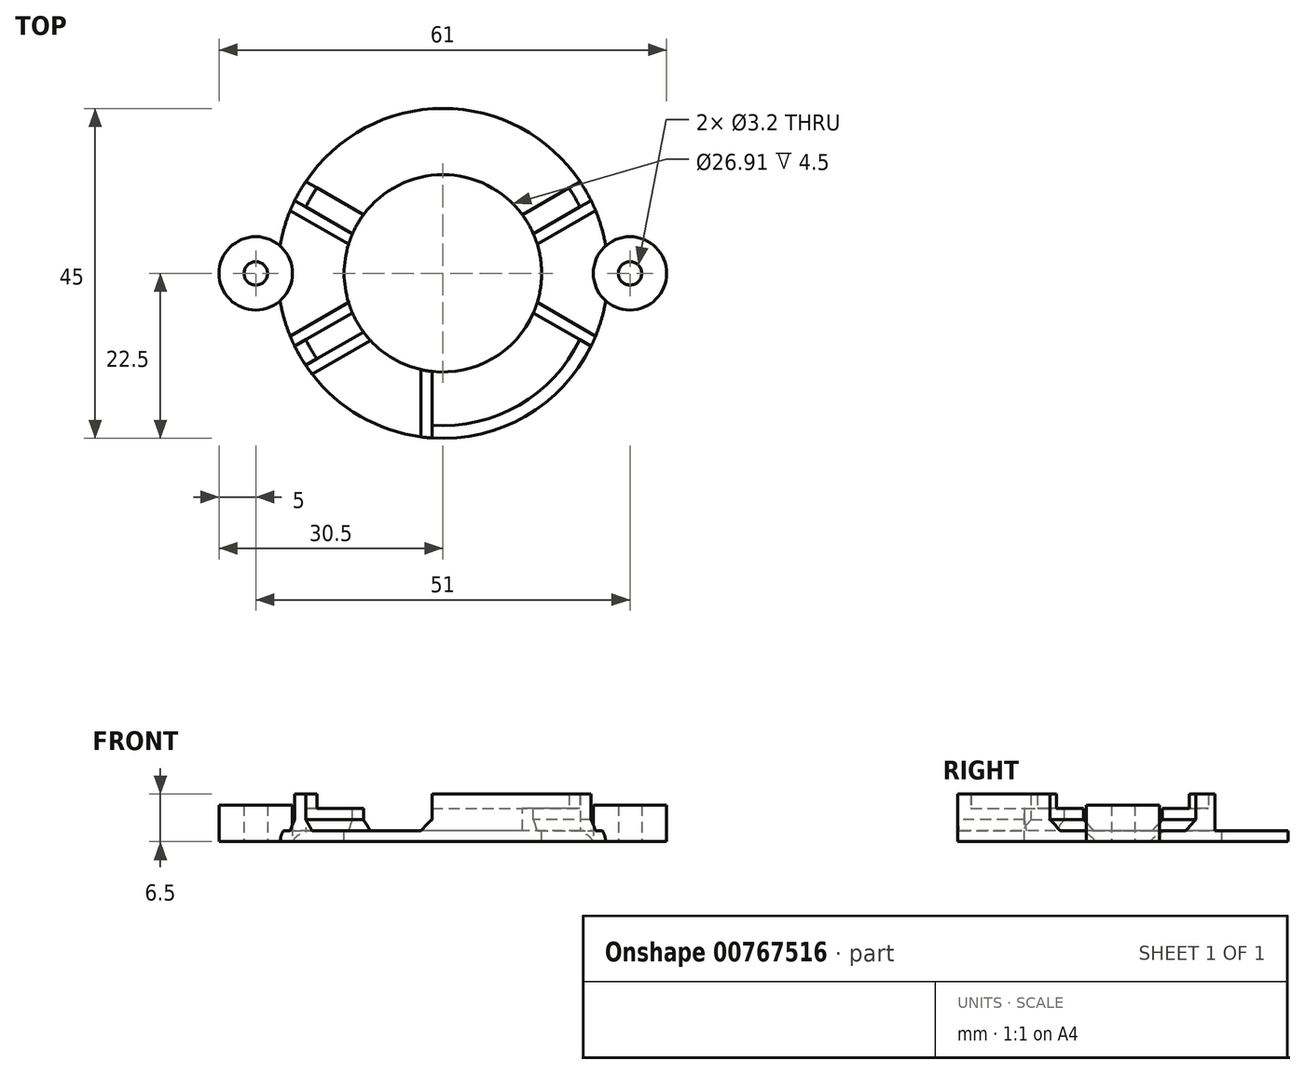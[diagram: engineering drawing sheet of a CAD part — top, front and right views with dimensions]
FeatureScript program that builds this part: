
annotation { "Feature Type Name" : "Feature", "Feature Type Description" : "" }
export const myFeature = defineFeature(function(context is Context, id is Id, definition is map)
    precondition{}
    {
        {
            var Q0;
            Q0=qCreatedBy(makeId("Top.planeOp"),FACE);
            var sketch = newSketch(context, id + "F0", { "sketchPlane" : qUnion([Q0])});
            skCircle(sketch, "E0", {"center": v(0, 0) * mm, "radius": 22.5 * mm});
            skCircle(sketch, "E1", {"center": v(25.5, 0) * mm, "radius": 5 * mm});
            skCircle(sketch, "E2", {"center": v(25.5, 0) * mm, "radius": 1.6 * mm});
            skCircle(sketch, "E3.1.0", {"center": v(-25.5, 0) * mm, "radius": 5 * mm});
            skCircle(sketch, "E3.1.1", {"center": v(-25.5, 0) * mm, "radius": 1.6 * mm});
            skSolve(sketch);
        }
        {
            var Q0;
            Q0=makeQuery(id+"F0.imprint","IMPRINT",FACE,{"disambiguationData":[TD([[makeQuery(id+"F0.imprint","IMPRINT",EDGE,{"derivedFrom":sQuery(id+"F0.wireOp",EDGE,"E3.1.1")}),-1.0]])]});
            var Q1;
            {var subQ0=sQuery(id+"F0.wireOp",EDGE,"E3.1.0");var subQ1=sQuery(id+"F0.wireOp",EDGE,"E0");var subQ2=makeQuery(id+"F0.imprint","INTERSECT",VERTEX,{"disambiguationData":[OD(0.0)],"derivedFrom":[subQ1,subQ0]});Q1=makeQuery(id+"F0.imprint","IMPRINT",FACE,{"disambiguationData":[TD([[makeQuery(id+"F0.imprint","IMPRINT",EDGE,{"disambiguationData":[TD([[subQ2,-1.0]])],"derivedFrom":subQ1}),1.0]])]});}
            var Q2;
            Q2=makeQuery(id+"F0.imprint","IMPRINT",FACE,{"disambiguationData":[TD([[makeQuery(id+"F0.imprint","IMPRINT",EDGE,{"derivedFrom":sQuery(id+"F0.wireOp",EDGE,"E2")}),-1.0]])]});
            var Q3;
            {var subQ0=sQuery(id+"F0.wireOp",EDGE,"E1");var subQ1=sQuery(id+"F0.wireOp",EDGE,"E0");var subQ2=makeQuery(id+"F0.imprint","INTERSECT",VERTEX,{"disambiguationData":[OD(0.0)],"derivedFrom":[subQ1,subQ0]});Q3=makeQuery(id+"F0.imprint","IMPRINT",FACE,{"disambiguationData":[TD([[makeQuery(id+"F0.imprint","IMPRINT",EDGE,{"disambiguationData":[TD([[subQ2,1.0]])],"derivedFrom":subQ1}),1.0]])]});}
            extrude(context, id + "F1", {"entities" : qUnion([Q0, Q1, Q2, Q3]), "depth" : 5 * mm, "offsetDistance" : 25 * mm});
        }
        {
            var Q0;
            {var subQ0=sQuery(id+"F0.wireOp",EDGE,"E3.1.0");var subQ1=sQuery(id+"F0.wireOp",EDGE,"E0");var subQ2=makeQuery(id+"F0.imprint","INTERSECT",VERTEX,{"disambiguationData":[OD(0.0)],"derivedFrom":[subQ1,subQ0]});Q0=makeQuery(id+"F0.imprint","IMPRINT",FACE,{"disambiguationData":[TD([[makeQuery(id+"F0.imprint","IMPRINT",EDGE,{"disambiguationData":[TD([[subQ2,1.0]])],"derivedFrom":subQ1}),1.0]])]});}
            extrude(context, id + "F2", {"entities" : qUnion([Q0]), "depth" : 1.5 * mm, "offsetDistance" : 25 * mm});
        }
        {
            var Q0;
            Q0=makeQuery(id+"F2.opExtrude","CAP_FACE",FACE,{"disambiguationData":[OSD([sQuery(id+"F0.wireOp",EDGE,"E0"),sQuery(id+"F0.wireOp",EDGE,"E1"),sQuery(id+"F0.wireOp",EDGE,"E3.1.0")])],"isStart":false});
            var sketch = newSketch(context, id + "F3", { "sketchPlane" : qUnion([Q0])});
            skCircle(sketch, "E4", {"center": v(0, 0) * mm, "radius": 20.75 * mm});
            skCircle(sketch, "E5", {"center": v(0, 0) * mm, "radius": 22.5 * mm});
            skLineSegment(sketch, "E6.bottom", {"start": v(-1.5, -27.93) * mm, "end": v(1.5, -27.93) * mm});
            skLineSegment(sketch, "E6.top", {"start": v(-1.5, 27.93) * mm, "end": v(1.5, 27.93) * mm});
            skLineSegment(sketch, "E6.left", {"start": v(-1.5, -27.93) * mm, "end": v(-1.5, 27.93) * mm});
            skLineSegment(sketch, "E6.right", {"start": v(1.5, -27.93) * mm, "end": v(1.5, 27.93) * mm});
            skLineSegment(sketch, "E7.1.0", {"start": v(23.43, 15.26) * mm, "end": v(-24.93, -12.66) * mm});
            skLineSegment(sketch, "E7.1.1", {"start": v(24.93, 12.66) * mm, "end": v(-23.43, -15.26) * mm});
            skLineSegment(sketch, "E7.1.2", {"start": v(-23.43, -15.26) * mm, "end": v(-24.93, -12.66) * mm});
            skLineSegment(sketch, "E7.1.3", {"start": v(24.93, 12.66) * mm, "end": v(23.43, 15.26) * mm});
            skLineSegment(sketch, "E7.2.0", {"start": v(-24.93, 12.66) * mm, "end": v(23.43, -15.26) * mm});
            skLineSegment(sketch, "E7.2.1", {"start": v(-23.43, 15.26) * mm, "end": v(24.93, -12.66) * mm});
            skLineSegment(sketch, "E7.2.2", {"start": v(24.93, -12.66) * mm, "end": v(23.43, -15.26) * mm});
            skLineSegment(sketch, "E7.2.3", {"start": v(-23.43, 15.26) * mm, "end": v(-24.93, 12.66) * mm});
            skSolve(sketch);
        }
        {
            var Q0;
            {var subQ5=sQuery(id+"F3.wireOp",EDGE,"E4");var subQ7=sQuery(id+"F3.wireOp",EDGE,"E7.2.1");var subQ9=makeQuery(id+"F3.imprint","INTERSECT",VERTEX,{"disambiguationData":[OD(0.0)],"derivedFrom":[subQ5,subQ7]});Q0=makeQuery(id+"F3.imprint","IMPRINT",FACE,{"disambiguationData":[TD([[makeQuery(id+"F3.imprint","IMPRINT",EDGE,{"disambiguationData":[TD([[subQ9,-1.0]])],"derivedFrom":subQ5}),1.0]])]});}
            var Q1;
            {var subQ0=sQuery(id+"F3.wireOp",EDGE,"E6.right");var subQ1=sQuery(id+"F3.wireOp",EDGE,"E4");var subQ2=makeQuery(id+"F3.imprint","INTERSECT",VERTEX,{"disambiguationData":[OD(0.0)],"derivedFrom":[subQ1,subQ0]});Q1=makeQuery(id+"F3.imprint","IMPRINT",FACE,{"disambiguationData":[TD([[makeQuery(id+"F3.imprint","IMPRINT",EDGE,{"disambiguationData":[TD([[subQ2,-1.0]])],"derivedFrom":subQ1}),1.0]])]});}
            var Q2;
            {var subQ1=sQuery(id+"F3.wireOp",EDGE,"E4");var subQ5=sQuery(id+"F3.wireOp",EDGE,"E7.1.1");var subQ6=makeQuery(id+"F3.imprint","INTERSECT",VERTEX,{"disambiguationData":[OD(0.0)],"derivedFrom":[subQ1,subQ5]});Q2=makeQuery(id+"F3.imprint","IMPRINT",FACE,{"disambiguationData":[TD([[makeQuery(id+"F3.imprint","IMPRINT",EDGE,{"disambiguationData":[TD([[subQ6,-1.0]])],"derivedFrom":subQ1}),1.0]])]});}
            var Q3;
            {var subQ5=sQuery(id+"F3.wireOp",EDGE,"E7.2.0");var subQ7=sQuery(id+"F3.wireOp",EDGE,"E4");var subQ8=makeQuery(id+"F3.imprint","INTERSECT",VERTEX,{"disambiguationData":[OD(1.0)],"derivedFrom":[subQ7,subQ5]});Q3=makeQuery(id+"F3.imprint","IMPRINT",FACE,{"disambiguationData":[TD([[makeQuery(id+"F3.imprint","IMPRINT",EDGE,{"disambiguationData":[TD([[subQ8,-1.0]])],"derivedFrom":subQ7}),1.0]])]});}
            var Q4;
            {var subQ1=sQuery(id+"F3.wireOp",EDGE,"E4");var subQ6=sQuery(id+"F3.wireOp",EDGE,"E6.left");var subQ9=makeQuery(id+"F3.imprint","INTERSECT",VERTEX,{"disambiguationData":[OD(1.0)],"derivedFrom":[subQ1,subQ6]});Q4=makeQuery(id+"F3.imprint","IMPRINT",FACE,{"disambiguationData":[TD([[makeQuery(id+"F3.imprint","IMPRINT",EDGE,{"disambiguationData":[TD([[subQ9,-1.0]])],"derivedFrom":subQ1}),1.0]])]});}
            var Q5;
            {var subQ0=sQuery(id+"F3.wireOp",EDGE,"E7.1.0");var subQ1=sQuery(id+"F3.wireOp",EDGE,"E4");var subQ2=makeQuery(id+"F3.imprint","INTERSECT",VERTEX,{"disambiguationData":[OD(1.0)],"derivedFrom":[subQ1,subQ0]});Q5=makeQuery(id+"F3.imprint","IMPRINT",FACE,{"disambiguationData":[TD([[makeQuery(id+"F3.imprint","IMPRINT",EDGE,{"disambiguationData":[TD([[subQ2,-1.0]])],"derivedFrom":subQ1}),1.0]])]});}
            var Q6;
            {var subQ0=sQuery(id+"F3.wireOp",EDGE,"E7.1.0");var subQ1=sQuery(id+"F3.wireOp",EDGE,"E6.left");var subQ2=makeQuery(id+"F3.imprint","INTERSECT",VERTEX,{"derivedFrom":[subQ1,subQ0]});Q6=makeQuery(id+"F3.imprint","IMPRINT",FACE,{"disambiguationData":[TD([[makeQuery(id+"F3.imprint","IMPRINT",EDGE,{"disambiguationData":[TD([[subQ2,-1.0]])],"derivedFrom":subQ1}),-1.0]])]});}
            var Q7;
            {var subQ0=sQuery(id+"F3.wireOp",EDGE,"E7.1.1");var subQ1=sQuery(id+"F3.wireOp",EDGE,"E6.right");var subQ2=makeQuery(id+"F3.imprint","INTERSECT",VERTEX,{"derivedFrom":[subQ1,subQ0]});Q7=makeQuery(id+"F3.imprint","IMPRINT",FACE,{"disambiguationData":[TD([[makeQuery(id+"F3.imprint","IMPRINT",EDGE,{"disambiguationData":[TD([[subQ2,-1.0]])],"derivedFrom":subQ1}),-1.0]])]});}
            var Q8;
            {var subQ0=sQuery(id+"F3.wireOp",EDGE,"E7.2.1");var subQ1=sQuery(id+"F3.wireOp",EDGE,"E6.right");var subQ2=makeQuery(id+"F3.imprint","INTERSECT",VERTEX,{"derivedFrom":[subQ1,subQ0]});Q8=makeQuery(id+"F3.imprint","IMPRINT",FACE,{"disambiguationData":[TD([[makeQuery(id+"F3.imprint","IMPRINT",EDGE,{"disambiguationData":[TD([[subQ2,-1.0]])],"derivedFrom":subQ1}),1.0]])]});}
            var Q9;
            {var subQ0=sQuery(id+"F3.wireOp",EDGE,"E7.2.0");var subQ1=sQuery(id+"F3.wireOp",EDGE,"E6.right");var subQ2=makeQuery(id+"F3.imprint","INTERSECT",VERTEX,{"derivedFrom":[subQ1,subQ0]});Q9=makeQuery(id+"F3.imprint","IMPRINT",FACE,{"disambiguationData":[TD([[makeQuery(id+"F3.imprint","IMPRINT",EDGE,{"disambiguationData":[TD([[subQ2,-1.0]])],"derivedFrom":subQ1}),1.0]])]});}
            var Q10;
            {var subQ0=sQuery(id+"F3.wireOp",EDGE,"E7.1.1");var subQ1=sQuery(id+"F3.wireOp",EDGE,"E6.left");var subQ2=makeQuery(id+"F3.imprint","INTERSECT",VERTEX,{"derivedFrom":[subQ1,subQ0]});Q10=makeQuery(id+"F3.imprint","IMPRINT",FACE,{"disambiguationData":[TD([[makeQuery(id+"F3.imprint","IMPRINT",EDGE,{"disambiguationData":[TD([[subQ2,-1.0]])],"derivedFrom":subQ1}),-1.0]])]});}
            var Q11;
            {var subQ0=sQuery(id+"F3.wireOp",EDGE,"E7.2.0");var subQ1=sQuery(id+"F3.wireOp",EDGE,"E6.left");var subQ2=makeQuery(id+"F3.imprint","INTERSECT",VERTEX,{"derivedFrom":[subQ1,subQ0]});Q11=makeQuery(id+"F3.imprint","IMPRINT",FACE,{"disambiguationData":[TD([[makeQuery(id+"F3.imprint","IMPRINT",EDGE,{"disambiguationData":[TD([[subQ2,-1.0]])],"derivedFrom":subQ1}),1.0]])]});}
            var Q12;
            {var subQ3=sQuery(id+"F3.wireOp",EDGE,"E7.2.0");var subQ5=sQuery(id+"F3.wireOp",EDGE,"E6.left");var subQ6=makeQuery(id+"F3.imprint","INTERSECT",VERTEX,{"derivedFrom":[subQ5,subQ3]});Q12=makeQuery(id+"F3.imprint","IMPRINT",FACE,{"disambiguationData":[TD([[makeQuery(id+"F3.imprint","IMPRINT",EDGE,{"disambiguationData":[TD([[subQ6,-1.0]])],"derivedFrom":subQ5}),-1.0]])]});}
            extrude(context, id + "F4", {"entities" : qUnion([Q0, Q1, Q2, Q3, Q4, Q5, Q6, Q7, Q8, Q9, Q10, Q11, Q12]), "operationType" : NewBodyOperationType.ADD, "depth" : 3 * mm, "offsetDistance" : 25 * mm});
        }
        {
            var Q0;
            {var subQ0=sQuery(id+"F3.wireOp",EDGE,"E6.right");var subQ1=sQuery(id+"F3.wireOp",EDGE,"E4");var subQ2=makeQuery(id+"F3.imprint","INTERSECT",VERTEX,{"disambiguationData":[OD(0.0)],"derivedFrom":[subQ1,subQ0]});Q0=makeQuery(id+"F3.imprint","IMPRINT",FACE,{"disambiguationData":[TD([[makeQuery(id+"F3.imprint","IMPRINT",EDGE,{"disambiguationData":[TD([[subQ2,-1.0]])],"derivedFrom":subQ1}),-1.0]])]});}
            var Q1;
            {var subQ0=sQuery(id+"F3.wireOp",EDGE,"E7.1.1");var subQ1=sQuery(id+"F3.wireOp",EDGE,"E4");var subQ2=makeQuery(id+"F3.imprint","INTERSECT",VERTEX,{"disambiguationData":[OD(0.0)],"derivedFrom":[subQ1,subQ0]});Q1=makeQuery(id+"F3.imprint","IMPRINT",FACE,{"disambiguationData":[TD([[makeQuery(id+"F3.imprint","IMPRINT",EDGE,{"disambiguationData":[TD([[subQ2,-1.0]])],"derivedFrom":subQ1}),-1.0]])]});}
            var Q2;
            {var subQ0=sQuery(id+"F3.wireOp",EDGE,"E7.2.0");var subQ1=sQuery(id+"F3.wireOp",EDGE,"E4");var subQ2=makeQuery(id+"F3.imprint","INTERSECT",VERTEX,{"disambiguationData":[OD(1.0)],"derivedFrom":[subQ1,subQ0]});Q2=makeQuery(id+"F3.imprint","IMPRINT",FACE,{"disambiguationData":[TD([[makeQuery(id+"F3.imprint","IMPRINT",EDGE,{"disambiguationData":[TD([[subQ2,-1.0]])],"derivedFrom":subQ1}),-1.0]])]});}
            var Q3;
            {var subQ0=sQuery(id+"F3.wireOp",EDGE,"E6.left");var subQ1=sQuery(id+"F3.wireOp",EDGE,"E4");var subQ2=makeQuery(id+"F3.imprint","INTERSECT",VERTEX,{"disambiguationData":[OD(1.0)],"derivedFrom":[subQ1,subQ0]});Q3=makeQuery(id+"F3.imprint","IMPRINT",FACE,{"disambiguationData":[TD([[makeQuery(id+"F3.imprint","IMPRINT",EDGE,{"disambiguationData":[TD([[subQ2,-1.0]])],"derivedFrom":subQ1}),-1.0]])]});}
            var Q4;
            {var subQ0=sQuery(id+"F3.wireOp",EDGE,"E7.1.0");var subQ1=sQuery(id+"F3.wireOp",EDGE,"E4");var subQ2=makeQuery(id+"F3.imprint","INTERSECT",VERTEX,{"disambiguationData":[OD(1.0)],"derivedFrom":[subQ1,subQ0]});Q4=makeQuery(id+"F3.imprint","IMPRINT",FACE,{"disambiguationData":[TD([[makeQuery(id+"F3.imprint","IMPRINT",EDGE,{"disambiguationData":[TD([[subQ2,-1.0]])],"derivedFrom":subQ1}),-1.0]])]});}
            var Q5;
            {var subQ0=sQuery(id+"F3.wireOp",EDGE,"E7.2.1");var subQ1=sQuery(id+"F3.wireOp",EDGE,"E4");var subQ2=makeQuery(id+"F3.imprint","INTERSECT",VERTEX,{"disambiguationData":[OD(0.0)],"derivedFrom":[subQ1,subQ0]});Q5=makeQuery(id+"F3.imprint","IMPRINT",FACE,{"disambiguationData":[TD([[makeQuery(id+"F3.imprint","IMPRINT",EDGE,{"disambiguationData":[TD([[subQ2,-1.0]])],"derivedFrom":subQ1}),-1.0]])]});}
            extrude(context, id + "F5", {"entities" : qUnion([Q0, Q1, Q2, Q3, Q4, Q5]), "operationType" : NewBodyOperationType.ADD, "depth" : 5 * mm, "offsetDistance" : 25 * mm});
        }
        {
            var Q0;
            Q0=makeQuery(id+"F2.opExtrude","CAP_EDGE",EDGE,{"disambiguationData":[OSD([sQuery(id+"F0.wireOp",EDGE,"E3.1.0")])],"isStart":false});
            var Q1;
            Q1=makeQuery(id+"F2.opExtrude","CAP_EDGE",EDGE,{"disambiguationData":[OSD([sQuery(id+"F0.wireOp",EDGE,"E1")])],"isStart":false});
            fillet(context, id + "F6", {"entities" : qUnion([Q0, Q1]), "radius" : 3 * mm, "tangentPropagation" : true, "allowEdgeOverflow" : false});
        }
        {
            var Q0;
            Q0=makeQuery(id+"F4.opExtrude","CAP_FACE",FACE,{"disambiguationData":[OSD([sQuery(id+"F3.wireOp",EDGE,"E4"),sQuery(id+"F3.wireOp",EDGE,"E6.left"),sQuery(id+"F3.wireOp",EDGE,"E6.right"),sQuery(id+"F3.wireOp",EDGE,"E7.1.0"),sQuery(id+"F3.wireOp",EDGE,"E7.1.1"),sQuery(id+"F3.wireOp",EDGE,"E7.2.0"),sQuery(id+"F3.wireOp",EDGE,"E7.2.1")])],"isStart":false});
            var sketch = newSketch(context, id + "F7", { "sketchPlane" : qUnion([Q0])});
            skCircle(sketch, "E8", {"center": v(0, 0) * mm, "radius": 13.46 * mm});
            skSolve(sketch);
        }
        {
            var Q0;
            {var subQ0=sQuery(id+"F7.wireOp",EDGE,"E8");var subQ1=sQuery(id+"F3.wireOp",EDGE,"E6.left");var subQ2=sQuery(id+"F3.wireOp",EDGE,"E4");var subQ5=makeQuery(id+"F4.opExtrude","CAP_EDGE",EDGE,{"disambiguationData":[OSD([subQ1]),TDD([makeQuery(id+"F3.imprint","IMPRINT",EDGE,{"disambiguationData":[TD([[makeQuery(id+"F3.imprint","INTERSECT",VERTEX,{"disambiguationData":[OD(0.0)],"derivedFrom":[subQ2,subQ1]}),1.0]])],"derivedFrom":subQ1})])],"isStart":false});var subQ6=makeQuery(id+"F7.imprint","INTERSECT",VERTEX,{"derivedFrom":[subQ5,subQ0]});Q0=makeQuery(id+"F7.imprint","IMPRINT",FACE,{"disambiguationData":[TD([[makeQuery(id+"F7.imprint","IMPRINT",EDGE,{"disambiguationData":[TD([[subQ6,-1.0]])],"derivedFrom":subQ0}),1.0]])]});}
            var Q1;
            {var subQ0=sQuery(id+"F3.wireOp",EDGE,"E7.1.0");var subQ1=sQuery(id+"F3.wireOp",EDGE,"E4");var subQ4=makeQuery(id+"F4.opExtrude","CAP_EDGE",EDGE,{"disambiguationData":[OSD([subQ0]),TDD([makeQuery(id+"F3.imprint","IMPRINT",EDGE,{"disambiguationData":[TD([[makeQuery(id+"F3.imprint","INTERSECT",VERTEX,{"disambiguationData":[OD(0.0)],"derivedFrom":[subQ1,subQ0]}),-1.0]])],"derivedFrom":subQ0})])],"isStart":false});var subQ7=sQuery(id+"F7.wireOp",EDGE,"E8");var subQ20=makeQuery(id+"F7.imprint","INTERSECT",VERTEX,{"derivedFrom":[subQ4,subQ7]});Q1=makeQuery(id+"F7.imprint","IMPRINT",FACE,{"disambiguationData":[TD([[makeQuery(id+"F7.imprint","IMPRINT",EDGE,{"disambiguationData":[TD([[subQ20,1.0]])],"derivedFrom":subQ7}),1.0]])]});}
            var Q2;
            {var subQ0=sQuery(id+"F7.wireOp",EDGE,"E8");var subQ1=sQuery(id+"F3.wireOp",EDGE,"E7.1.0");var subQ2=sQuery(id+"F3.wireOp",EDGE,"E4");var subQ5=makeQuery(id+"F4.opExtrude","CAP_EDGE",EDGE,{"disambiguationData":[OSD([subQ1]),TDD([makeQuery(id+"F3.imprint","IMPRINT",EDGE,{"disambiguationData":[TD([[makeQuery(id+"F3.imprint","INTERSECT",VERTEX,{"disambiguationData":[OD(0.0)],"derivedFrom":[subQ2,subQ1]}),-1.0]])],"derivedFrom":subQ1})])],"isStart":false});var subQ6=makeQuery(id+"F7.imprint","INTERSECT",VERTEX,{"derivedFrom":[subQ5,subQ0]});Q2=makeQuery(id+"F7.imprint","IMPRINT",FACE,{"disambiguationData":[TD([[makeQuery(id+"F7.imprint","IMPRINT",EDGE,{"disambiguationData":[TD([[subQ6,-1.0]])],"derivedFrom":subQ0}),1.0]])]});}
            var Q3;
            {var subQ0=sQuery(id+"F7.wireOp",EDGE,"E8");var subQ1=sQuery(id+"F3.wireOp",EDGE,"E7.1.1");var subQ2=sQuery(id+"F3.wireOp",EDGE,"E4");var subQ5=makeQuery(id+"F4.opExtrude","CAP_EDGE",EDGE,{"disambiguationData":[OSD([subQ1]),TDD([makeQuery(id+"F3.imprint","IMPRINT",EDGE,{"disambiguationData":[TD([[makeQuery(id+"F3.imprint","INTERSECT",VERTEX,{"disambiguationData":[OD(0.0)],"derivedFrom":[subQ2,subQ1]}),-1.0]])],"derivedFrom":subQ1})])],"isStart":false});var subQ6=makeQuery(id+"F7.imprint","INTERSECT",VERTEX,{"derivedFrom":[subQ5,subQ0]});Q3=makeQuery(id+"F7.imprint","IMPRINT",FACE,{"disambiguationData":[TD([[makeQuery(id+"F7.imprint","IMPRINT",EDGE,{"disambiguationData":[TD([[subQ6,1.0]])],"derivedFrom":subQ0}),1.0]])]});}
            var Q4;
            {var subQ0=sQuery(id+"F7.wireOp",EDGE,"E8");var subQ1=sQuery(id+"F3.wireOp",EDGE,"E6.right");var subQ2=sQuery(id+"F3.wireOp",EDGE,"E4");var subQ5=makeQuery(id+"F4.opExtrude","CAP_EDGE",EDGE,{"disambiguationData":[OSD([subQ1]),TDD([makeQuery(id+"F3.imprint","IMPRINT",EDGE,{"disambiguationData":[TD([[makeQuery(id+"F3.imprint","INTERSECT",VERTEX,{"disambiguationData":[OD(1.0)],"derivedFrom":[subQ2,subQ1]}),-1.0]])],"derivedFrom":subQ1})])],"isStart":false});var subQ6=makeQuery(id+"F7.imprint","INTERSECT",VERTEX,{"derivedFrom":[subQ5,subQ0]});Q4=makeQuery(id+"F7.imprint","IMPRINT",FACE,{"disambiguationData":[TD([[makeQuery(id+"F7.imprint","IMPRINT",EDGE,{"disambiguationData":[TD([[subQ6,-1.0]])],"derivedFrom":subQ0}),1.0]])]});}
            var Q5;
            {var subQ0=sQuery(id+"F7.wireOp",EDGE,"E8");var subQ1=sQuery(id+"F3.wireOp",EDGE,"E7.1.1");var subQ2=sQuery(id+"F3.wireOp",EDGE,"E4");var subQ5=makeQuery(id+"F4.opExtrude","CAP_EDGE",EDGE,{"disambiguationData":[OSD([subQ1]),TDD([makeQuery(id+"F3.imprint","IMPRINT",EDGE,{"disambiguationData":[TD([[makeQuery(id+"F3.imprint","INTERSECT",VERTEX,{"disambiguationData":[OD(1.0)],"derivedFrom":[subQ2,subQ1]}),1.0]])],"derivedFrom":subQ1})])],"isStart":false});var subQ6=makeQuery(id+"F7.imprint","INTERSECT",VERTEX,{"derivedFrom":[subQ5,subQ0]});Q5=makeQuery(id+"F7.imprint","IMPRINT",FACE,{"disambiguationData":[TD([[makeQuery(id+"F7.imprint","IMPRINT",EDGE,{"disambiguationData":[TD([[subQ6,-1.0]])],"derivedFrom":subQ0}),1.0]])]});}
            var Q6;
            {var subQ0=sQuery(id+"F7.wireOp",EDGE,"E8");var subQ1=sQuery(id+"F3.wireOp",EDGE,"E7.2.0");var subQ2=sQuery(id+"F3.wireOp",EDGE,"E4");var subQ5=makeQuery(id+"F4.opExtrude","CAP_EDGE",EDGE,{"disambiguationData":[OSD([subQ1]),TDD([makeQuery(id+"F3.imprint","IMPRINT",EDGE,{"disambiguationData":[TD([[makeQuery(id+"F3.imprint","INTERSECT",VERTEX,{"disambiguationData":[OD(0.0)],"derivedFrom":[subQ2,subQ1]}),-1.0]])],"derivedFrom":subQ1})])],"isStart":false});var subQ6=makeQuery(id+"F7.imprint","INTERSECT",VERTEX,{"derivedFrom":[subQ5,subQ0]});Q6=makeQuery(id+"F7.imprint","IMPRINT",FACE,{"disambiguationData":[TD([[makeQuery(id+"F7.imprint","IMPRINT",EDGE,{"disambiguationData":[TD([[subQ6,-1.0]])],"derivedFrom":subQ0}),1.0]])]});}
            extrude(context, id + "F8", {"entities" : qUnion([Q0, Q1, Q2, Q3, Q4, Q5, Q6]), "operationType" : NewBodyOperationType.REMOVE, "oppositeDirection" : true, "depth" : 25 * mm, "offsetDistance" : 25 * mm});
        }
        {
            var Q0;
            {var subQ0=sQuery(id+"F3.wireOp",EDGE,"E6.right");var subQ1=makeQuery(id+"F3.imprint","INTERSECT",VERTEX,{"disambiguationData":[OD(0.0)],"derivedFrom":[sQuery(id+"F3.wireOp",EDGE,"E4"),subQ0]});Q0=makeQuery(id+"F5.boolean.opBoolean","MERGE",EDGE,{"derivedFrom":[makeQuery(id+"F4.opExtrude","CAP_EDGE",EDGE,{"disambiguationData":[OSD([subQ0]),TDD([makeQuery(id+"F3.imprint","IMPRINT",EDGE,{"disambiguationData":[TD([[subQ1,1.0]])],"derivedFrom":subQ0})])],"isStart":true}),makeQuery(id+"F5.opExtrude","CAP_EDGE",EDGE,{"disambiguationData":[OSD([subQ0]),TDD([makeQuery(id+"F3.imprint","IMPRINT",EDGE,{"disambiguationData":[TD([[makeQuery(id+"F3.imprint","INTERSECT",VERTEX,{"disambiguationData":[OD(0.0)],"derivedFrom":[sQuery(id+"F3.wireOp",EDGE,"E5"),subQ0]}),1.0]])],"derivedFrom":subQ0})])],"isStart":true})]});}
            var Q1;
            {var subQ0=sQuery(id+"F3.wireOp",EDGE,"E7.2.1");var subQ1=makeQuery(id+"F3.imprint","INTERSECT",VERTEX,{"disambiguationData":[OD(0.0)],"derivedFrom":[sQuery(id+"F3.wireOp",EDGE,"E4"),subQ0]});Q1=makeQuery(id+"F5.boolean.opBoolean","MERGE",EDGE,{"derivedFrom":[makeQuery(id+"F4.opExtrude","CAP_EDGE",EDGE,{"disambiguationData":[OSD([subQ0]),TDD([makeQuery(id+"F3.imprint","IMPRINT",EDGE,{"disambiguationData":[TD([[subQ1,-1.0]])],"derivedFrom":subQ0})])],"isStart":true}),makeQuery(id+"F5.opExtrude","CAP_EDGE",EDGE,{"disambiguationData":[OSD([subQ0]),TDD([makeQuery(id+"F3.imprint","IMPRINT",EDGE,{"disambiguationData":[TD([[makeQuery(id+"F3.imprint","INTERSECT",VERTEX,{"disambiguationData":[OD(0.0)],"derivedFrom":[sQuery(id+"F3.wireOp",EDGE,"E5"),subQ0]}),-1.0]])],"derivedFrom":subQ0})])],"isStart":true})]});}
            var Q2;
            {var subQ0=sQuery(id+"F3.wireOp",EDGE,"E7.1.1");var subQ1=makeQuery(id+"F3.imprint","INTERSECT",VERTEX,{"disambiguationData":[OD(1.0)],"derivedFrom":[sQuery(id+"F3.wireOp",EDGE,"E4"),subQ0]});Q2=makeQuery(id+"F5.boolean.opBoolean","MERGE",EDGE,{"derivedFrom":[makeQuery(id+"F4.opExtrude","CAP_EDGE",EDGE,{"disambiguationData":[OSD([subQ0]),TDD([makeQuery(id+"F3.imprint","IMPRINT",EDGE,{"disambiguationData":[TD([[subQ1,1.0]])],"derivedFrom":subQ0})])],"isStart":true}),makeQuery(id+"F5.opExtrude","CAP_EDGE",EDGE,{"disambiguationData":[OSD([subQ0]),TDD([makeQuery(id+"F3.imprint","IMPRINT",EDGE,{"disambiguationData":[TD([[makeQuery(id+"F3.imprint","INTERSECT",VERTEX,{"disambiguationData":[OD(1.0)],"derivedFrom":[sQuery(id+"F3.wireOp",EDGE,"E5"),subQ0]}),1.0]])],"derivedFrom":subQ0})])],"isStart":true})]});}
            var Q3;
            {var subQ0=sQuery(id+"F3.wireOp",EDGE,"E6.right");var subQ1=makeQuery(id+"F3.imprint","INTERSECT",VERTEX,{"disambiguationData":[OD(1.0)],"derivedFrom":[sQuery(id+"F3.wireOp",EDGE,"E4"),subQ0]});Q3=makeQuery(id+"F5.boolean.opBoolean","MERGE",EDGE,{"derivedFrom":[makeQuery(id+"F4.opExtrude","CAP_EDGE",EDGE,{"disambiguationData":[OSD([subQ0]),TDD([makeQuery(id+"F3.imprint","IMPRINT",EDGE,{"disambiguationData":[TD([[subQ1,-1.0]])],"derivedFrom":subQ0})])],"isStart":true}),makeQuery(id+"F5.opExtrude","CAP_EDGE",EDGE,{"disambiguationData":[OSD([subQ0]),TDD([makeQuery(id+"F3.imprint","IMPRINT",EDGE,{"disambiguationData":[TD([[makeQuery(id+"F3.imprint","INTERSECT",VERTEX,{"disambiguationData":[OD(1.0)],"derivedFrom":[sQuery(id+"F3.wireOp",EDGE,"E5"),subQ0]}),-1.0]])],"derivedFrom":subQ0})])],"isStart":true})]});}
            var Q4;
            {var subQ0=sQuery(id+"F3.wireOp",EDGE,"E7.2.1");var subQ1=makeQuery(id+"F3.imprint","INTERSECT",VERTEX,{"disambiguationData":[OD(1.0)],"derivedFrom":[sQuery(id+"F3.wireOp",EDGE,"E4"),subQ0]});Q4=makeQuery(id+"F5.boolean.opBoolean","MERGE",EDGE,{"derivedFrom":[makeQuery(id+"F4.opExtrude","CAP_EDGE",EDGE,{"disambiguationData":[OSD([subQ0]),TDD([makeQuery(id+"F3.imprint","IMPRINT",EDGE,{"disambiguationData":[TD([[subQ1,1.0]])],"derivedFrom":subQ0})])],"isStart":true}),makeQuery(id+"F5.opExtrude","CAP_EDGE",EDGE,{"disambiguationData":[OSD([subQ0]),TDD([makeQuery(id+"F3.imprint","IMPRINT",EDGE,{"disambiguationData":[TD([[makeQuery(id+"F3.imprint","INTERSECT",VERTEX,{"disambiguationData":[OD(1.0)],"derivedFrom":[sQuery(id+"F3.wireOp",EDGE,"E5"),subQ0]}),1.0]])],"derivedFrom":subQ0})])],"isStart":true})]});}
            var Q5;
            {var subQ0=sQuery(id+"F3.wireOp",EDGE,"E7.1.1");var subQ1=makeQuery(id+"F3.imprint","INTERSECT",VERTEX,{"disambiguationData":[OD(0.0)],"derivedFrom":[sQuery(id+"F3.wireOp",EDGE,"E4"),subQ0]});Q5=makeQuery(id+"F5.boolean.opBoolean","MERGE",EDGE,{"derivedFrom":[makeQuery(id+"F4.opExtrude","CAP_EDGE",EDGE,{"disambiguationData":[OSD([subQ0]),TDD([makeQuery(id+"F3.imprint","IMPRINT",EDGE,{"disambiguationData":[TD([[subQ1,-1.0]])],"derivedFrom":subQ0})])],"isStart":true}),makeQuery(id+"F5.opExtrude","CAP_EDGE",EDGE,{"disambiguationData":[OSD([subQ0]),TDD([makeQuery(id+"F3.imprint","IMPRINT",EDGE,{"disambiguationData":[TD([[makeQuery(id+"F3.imprint","INTERSECT",VERTEX,{"disambiguationData":[OD(0.0)],"derivedFrom":[sQuery(id+"F3.wireOp",EDGE,"E5"),subQ0]}),-1.0]])],"derivedFrom":subQ0})])],"isStart":true})]});}
            var Q6;
            {var subQ0=sQuery(id+"F3.wireOp",EDGE,"E7.1.0");var subQ1=makeQuery(id+"F3.imprint","INTERSECT",VERTEX,{"disambiguationData":[OD(0.0)],"derivedFrom":[sQuery(id+"F3.wireOp",EDGE,"E4"),subQ0]});Q6=makeQuery(id+"F5.boolean.opBoolean","MERGE",EDGE,{"derivedFrom":[makeQuery(id+"F4.opExtrude","CAP_EDGE",EDGE,{"disambiguationData":[OSD([subQ0]),TDD([makeQuery(id+"F3.imprint","IMPRINT",EDGE,{"disambiguationData":[TD([[subQ1,-1.0]])],"derivedFrom":subQ0})])],"isStart":true}),makeQuery(id+"F5.opExtrude","CAP_EDGE",EDGE,{"disambiguationData":[OSD([subQ0]),TDD([makeQuery(id+"F3.imprint","IMPRINT",EDGE,{"disambiguationData":[TD([[makeQuery(id+"F3.imprint","INTERSECT",VERTEX,{"disambiguationData":[OD(0.0)],"derivedFrom":[sQuery(id+"F3.wireOp",EDGE,"E5"),subQ0]}),-1.0]])],"derivedFrom":subQ0})])],"isStart":true})]});}
            var Q7;
            {var subQ0=sQuery(id+"F3.wireOp",EDGE,"E6.left");var subQ1=makeQuery(id+"F3.imprint","INTERSECT",VERTEX,{"disambiguationData":[OD(0.0)],"derivedFrom":[sQuery(id+"F3.wireOp",EDGE,"E4"),subQ0]});Q7=makeQuery(id+"F5.boolean.opBoolean","MERGE",EDGE,{"derivedFrom":[makeQuery(id+"F4.opExtrude","CAP_EDGE",EDGE,{"disambiguationData":[OSD([subQ0]),TDD([makeQuery(id+"F3.imprint","IMPRINT",EDGE,{"disambiguationData":[TD([[subQ1,1.0]])],"derivedFrom":subQ0})])],"isStart":true}),makeQuery(id+"F5.opExtrude","CAP_EDGE",EDGE,{"disambiguationData":[OSD([subQ0]),TDD([makeQuery(id+"F3.imprint","IMPRINT",EDGE,{"disambiguationData":[TD([[makeQuery(id+"F3.imprint","INTERSECT",VERTEX,{"disambiguationData":[OD(0.0)],"derivedFrom":[sQuery(id+"F3.wireOp",EDGE,"E5"),subQ0]}),1.0]])],"derivedFrom":subQ0})])],"isStart":true})]});}
            var Q8;
            {var subQ0=sQuery(id+"F3.wireOp",EDGE,"E7.1.0");var subQ1=makeQuery(id+"F3.imprint","INTERSECT",VERTEX,{"disambiguationData":[OD(1.0)],"derivedFrom":[sQuery(id+"F3.wireOp",EDGE,"E4"),subQ0]});Q8=makeQuery(id+"F5.boolean.opBoolean","MERGE",EDGE,{"derivedFrom":[makeQuery(id+"F4.opExtrude","CAP_EDGE",EDGE,{"disambiguationData":[OSD([subQ0]),TDD([makeQuery(id+"F3.imprint","IMPRINT",EDGE,{"disambiguationData":[TD([[subQ1,1.0]])],"derivedFrom":subQ0})])],"isStart":true}),makeQuery(id+"F5.opExtrude","CAP_EDGE",EDGE,{"disambiguationData":[OSD([subQ0]),TDD([makeQuery(id+"F3.imprint","IMPRINT",EDGE,{"disambiguationData":[TD([[makeQuery(id+"F3.imprint","INTERSECT",VERTEX,{"disambiguationData":[OD(1.0)],"derivedFrom":[sQuery(id+"F3.wireOp",EDGE,"E5"),subQ0]}),1.0]])],"derivedFrom":subQ0})])],"isStart":true})]});}
            var Q9;
            {var subQ0=sQuery(id+"F3.wireOp",EDGE,"E6.left");var subQ1=makeQuery(id+"F3.imprint","INTERSECT",VERTEX,{"disambiguationData":[OD(1.0)],"derivedFrom":[sQuery(id+"F3.wireOp",EDGE,"E4"),subQ0]});Q9=makeQuery(id+"F5.boolean.opBoolean","MERGE",EDGE,{"derivedFrom":[makeQuery(id+"F4.opExtrude","CAP_EDGE",EDGE,{"disambiguationData":[OSD([subQ0]),TDD([makeQuery(id+"F3.imprint","IMPRINT",EDGE,{"disambiguationData":[TD([[subQ1,-1.0]])],"derivedFrom":subQ0})])],"isStart":true}),makeQuery(id+"F5.opExtrude","CAP_EDGE",EDGE,{"disambiguationData":[OSD([subQ0]),TDD([makeQuery(id+"F3.imprint","IMPRINT",EDGE,{"disambiguationData":[TD([[makeQuery(id+"F3.imprint","INTERSECT",VERTEX,{"disambiguationData":[OD(1.0)],"derivedFrom":[sQuery(id+"F3.wireOp",EDGE,"E5"),subQ0]}),-1.0]])],"derivedFrom":subQ0})])],"isStart":true})]});}
            var Q10;
            {var subQ0=sQuery(id+"F3.wireOp",EDGE,"E7.2.0");var subQ1=makeQuery(id+"F3.imprint","INTERSECT",VERTEX,{"disambiguationData":[OD(1.0)],"derivedFrom":[sQuery(id+"F3.wireOp",EDGE,"E4"),subQ0]});Q10=makeQuery(id+"F5.boolean.opBoolean","MERGE",EDGE,{"derivedFrom":[makeQuery(id+"F4.opExtrude","CAP_EDGE",EDGE,{"disambiguationData":[OSD([subQ0]),TDD([makeQuery(id+"F3.imprint","IMPRINT",EDGE,{"disambiguationData":[TD([[subQ1,1.0]])],"derivedFrom":subQ0})])],"isStart":true}),makeQuery(id+"F5.opExtrude","CAP_EDGE",EDGE,{"disambiguationData":[OSD([subQ0]),TDD([makeQuery(id+"F3.imprint","IMPRINT",EDGE,{"disambiguationData":[TD([[makeQuery(id+"F3.imprint","INTERSECT",VERTEX,{"disambiguationData":[OD(1.0)],"derivedFrom":[sQuery(id+"F3.wireOp",EDGE,"E5"),subQ0]}),1.0]])],"derivedFrom":subQ0})])],"isStart":true})]});}
            var Q11;
            {var subQ0=sQuery(id+"F3.wireOp",EDGE,"E7.2.0");var subQ1=makeQuery(id+"F3.imprint","INTERSECT",VERTEX,{"disambiguationData":[OD(0.0)],"derivedFrom":[sQuery(id+"F3.wireOp",EDGE,"E4"),subQ0]});Q11=makeQuery(id+"F5.boolean.opBoolean","MERGE",EDGE,{"derivedFrom":[makeQuery(id+"F4.opExtrude","CAP_EDGE",EDGE,{"disambiguationData":[OSD([subQ0]),TDD([makeQuery(id+"F3.imprint","IMPRINT",EDGE,{"disambiguationData":[TD([[subQ1,-1.0]])],"derivedFrom":subQ0})])],"isStart":true}),makeQuery(id+"F5.opExtrude","CAP_EDGE",EDGE,{"disambiguationData":[OSD([subQ0]),TDD([makeQuery(id+"F3.imprint","IMPRINT",EDGE,{"disambiguationData":[TD([[makeQuery(id+"F3.imprint","INTERSECT",VERTEX,{"disambiguationData":[OD(0.0)],"derivedFrom":[sQuery(id+"F3.wireOp",EDGE,"E5"),subQ0]}),-1.0]])],"derivedFrom":subQ0})])],"isStart":true})]});}
            chamfer(context, id + "F9", {"entities" : qUnion([Q0, Q1, Q2, Q3, Q4, Q5, Q6, Q7, Q8, Q9, Q10, Q11]), "width" : 1.5 * mm, "tangentPropagation" : true});
        }
    });
